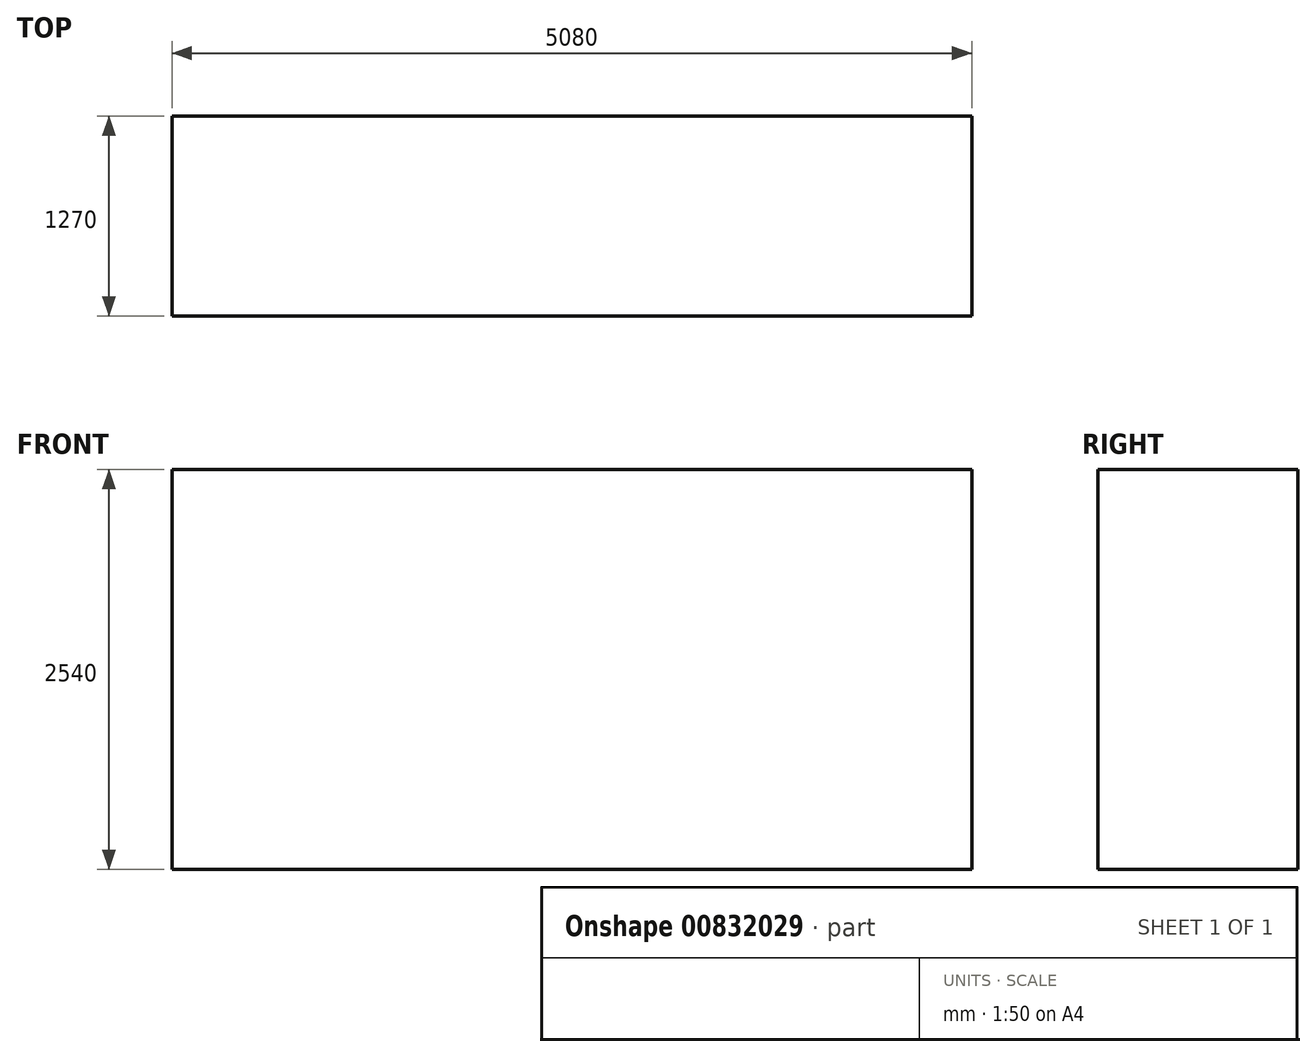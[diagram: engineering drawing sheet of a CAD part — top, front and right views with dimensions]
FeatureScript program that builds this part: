
annotation { "Feature Type Name" : "Feature", "Feature Type Description" : "" }
export const myFeature = defineFeature(function(context is Context, id is Id, definition is map)
    precondition{}
    {
        {
            var Q0;
            Q0=qCreatedBy(makeId("Front.planeOp"),FACE);
            var sketch = newSketch(context, id + "F0", { "sketchPlane" : qUnion([Q0])});
            skLineSegment(sketch, "E0.bottom", {"start": v(0, 0) * mm, "end": v(5080, 0) * mm});
            skLineSegment(sketch, "E0.top", {"start": v(0, 2540) * mm, "end": v(5080, 2540) * mm});
            skLineSegment(sketch, "E0.left", {"start": v(0, 0) * mm, "end": v(0, 2540) * mm});
            skLineSegment(sketch, "E0.right", {"start": v(5080, 0) * mm, "end": v(5080, 2540) * mm});
            skSolve(sketch);
        }
        {
            var Q0;
            Q0 = qSketchRegion(id + "F0", true);
            extrude(context, id + "F1", {"entities" : qUnion([Q0]), "depth" : 1270 * mm, "offsetDistance" : 25.4 * mm});
        }
    });
